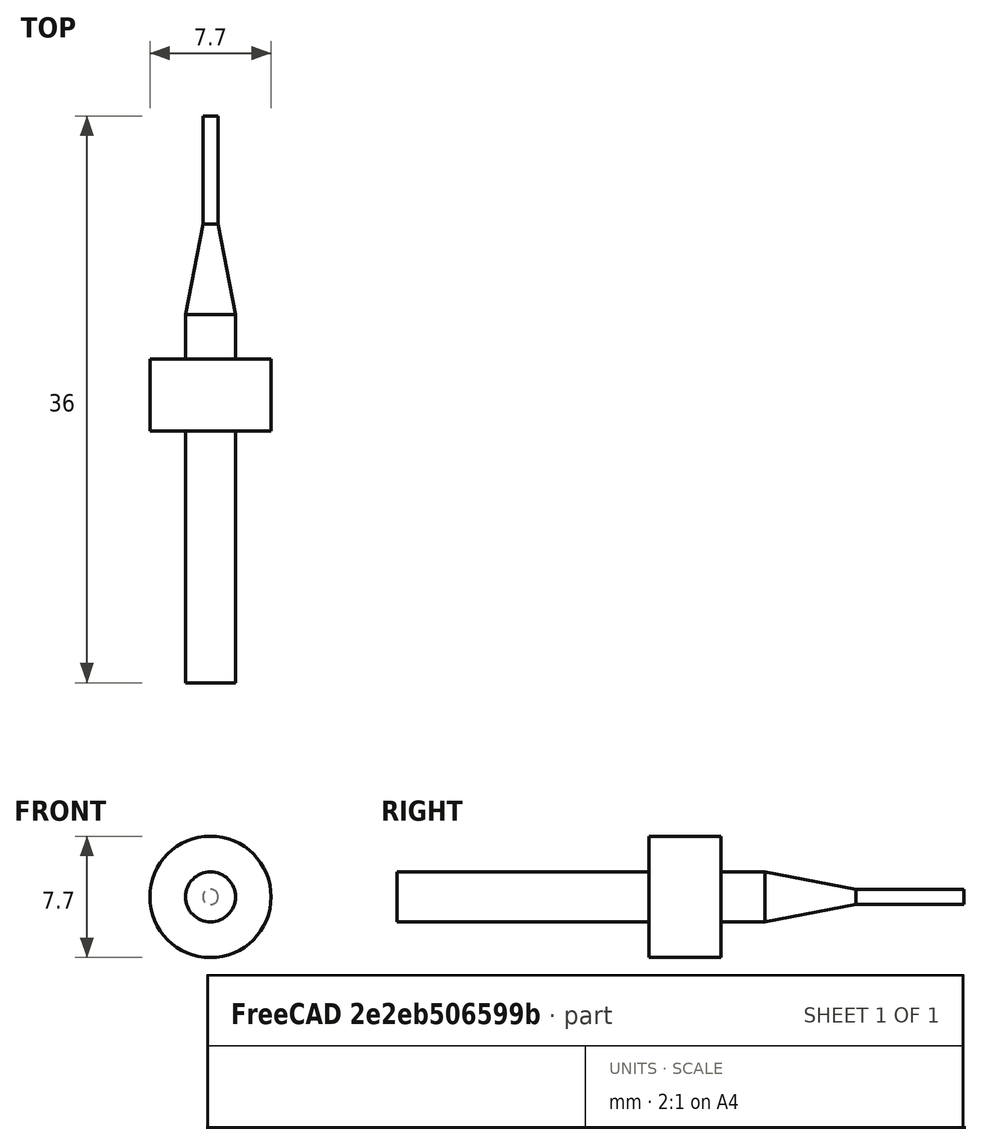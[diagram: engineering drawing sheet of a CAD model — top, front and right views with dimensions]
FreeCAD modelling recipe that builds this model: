
FCSTD DOCUMENT  (FreeCAD 0.18R)
Label: endmill
License: All rights reserved
LicenseURL: http://en.wikipedia.org/wiki/All_rights_reserved
objects: Sketcher::SketchObject×1, PartDesign::Revolution×1, PartDesign::Body×1
note: 4 computed .brp shape members not serialized (recipe doc carries the construction recipe); baked Part::Feature solids carry a one-line shape summary decoded from their .brp

FEATURE [Sketcher::SketchObject] Sketch
  MapMode = 5
  Support = -> [XY_Plane]
  sketch-geometry (11):
    g0: LineSegment StartX=-1.585 StartY=0 StartZ=0 EndX=-3.85 EndY=0 EndZ=0
    g1: LineSegment StartX=-3.85 StartY=0 StartZ=0 EndX=-3.85 EndY=4.56 EndZ=0
    g2: LineSegment StartX=-3.85 StartY=4.56 StartZ=0 EndX=-1.585 EndY=4.56 EndZ=0
    g3: LineSegment StartX=-1.585 StartY=4.56 StartZ=0 EndX=-1.585 EndY=7.38 EndZ=0
    g4: LineSegment StartX=-0.485 StartY=20 StartZ=0 EndX=0 EndY=20 EndZ=0
    g5: LineSegment StartX=0 StartY=20 StartZ=0 EndX=0 EndY=0 EndZ=0
    g6: LineSegment StartX=-0.485 StartY=20 StartZ=0 EndX=-0.485 EndY=13.14 EndZ=0
    g7: LineSegment StartX=-0.485 StartY=13.14 StartZ=0 EndX=-1.585 EndY=7.38 EndZ=0
    g8: LineSegment StartX=-1.585 StartY=0 StartZ=0 EndX=-1.585 EndY=-16 EndZ=0
    g9: LineSegment StartX=-1.585 StartY=-16 StartZ=0 EndX=0 EndY=-16 EndZ=0
    g10: LineSegment StartX=0 StartY=-16 StartZ=0 EndX=0 EndY=0 EndZ=0
  constraints (30):
    c: Horizontal(g0)
    c: DistanceX(g0,g-1) = 3.85
    c: Coincident(g1,g0)
    c: Vertical(g1)
    c: DistanceY(g1,g1) = 4.56
    c: Coincident(g2,g1)
    c: Horizontal(g2)
    c: DistanceX(g2,g-1) = 1.585
    c: Coincident(g3,g2)
    c: Vertical(g3)
    c: DistanceY(g3,g3) = 2.82
    c: PointOnObject(g4,g-2)
    c: Horizontal(g4)
    c: DistanceX(g4,g-1) = 0.485
    c: DistanceY(g-1,g4) = 20
    c: Coincident(g5,g4)
    c: Coincident(g5,g-1)
    c: Coincident(g6,g4)
    c: Vertical(g6)
    c: Coincident(g7,g6)
    c: Coincident(g7,g3)
    c: DistanceY(g3,g6) = 5.76
    c: Vertical(g8)
    c: Coincident(g9,g8)
    c: PointOnObject(g9,g-2)
    c: Coincident(g10,g-1)
    c: Horizontal(g9)
    c: Coincident(g9,g10)
    c: DistanceY(g9,g-1) = 16
    c: Coincident(g0,g8)
FEATURE [PartDesign::Revolution] Revolution  label="endmill"
  Angle = 360
  Axis = (0,1,0)
  Base = (0,0,0)
  Profile = -> Sketch
  ReferenceAxis = -> Sketch [V_Axis]
FEATURE [PartDesign::Body] Body  label="endmill001"
  Group = -> [Sketch,Revolution]
  Origin = -> Origin
  Tip = -> Revolution
